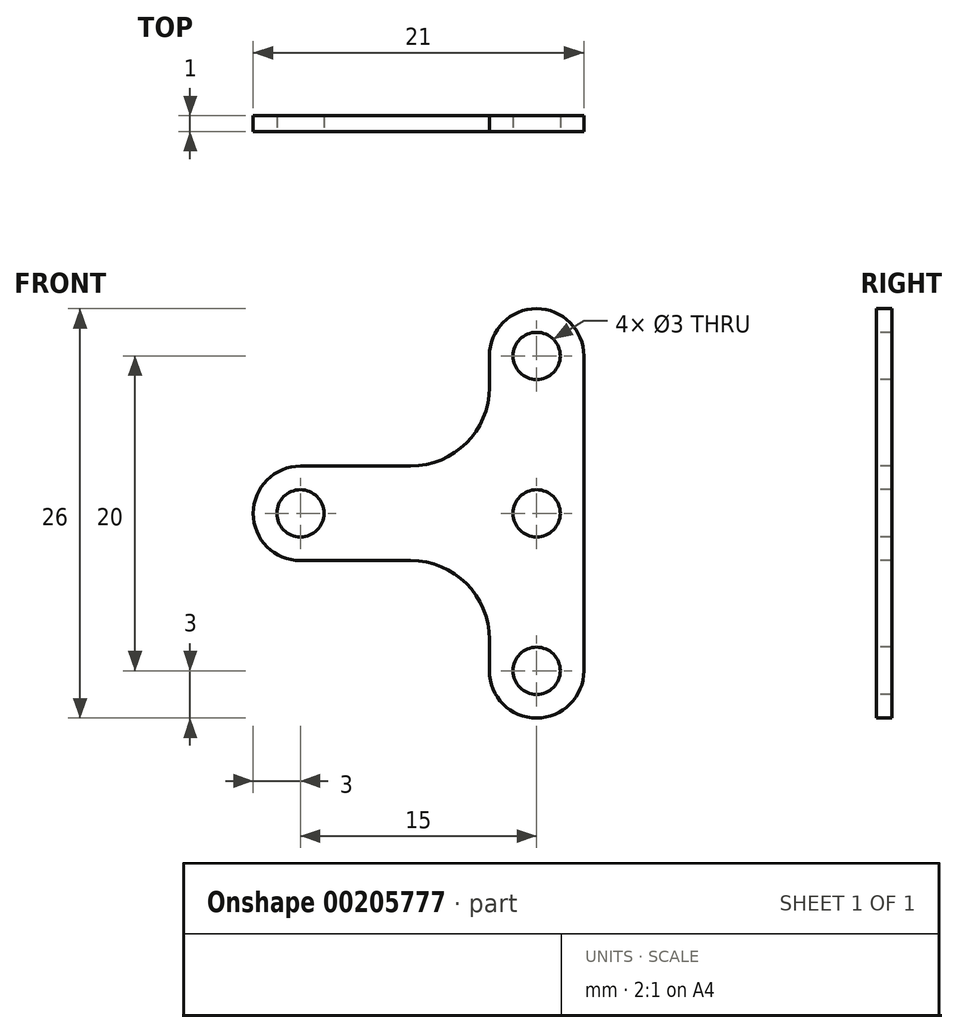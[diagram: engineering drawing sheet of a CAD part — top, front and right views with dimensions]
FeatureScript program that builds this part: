
annotation { "Feature Type Name" : "Feature", "Feature Type Description" : "" }
export const myFeature = defineFeature(function(context is Context, id is Id, definition is map)
    precondition{}
    {
        {
            var Q0;
            Q0=qCreatedBy(makeId("Front.planeOp"),FACE);
            var sketch = newSketch(context, id + "F0", { "sketchPlane" : qUnion([Q0])});
            skLineSegment(sketch, "E0", {"start": v(0, 10) * mm, "end": v(0, -10) * mm, "construction": true});
            skLineSegment(sketch, "E1", {"start": v(0, 0) * mm, "end": v(-15, 0) * mm, "construction": true});
            skCircle(sketch, "E2", {"center": v(0, 10) * mm, "radius": 1.5 * mm});
            skCircle(sketch, "E3", {"center": v(0, -10) * mm, "radius": 1.5 * mm});
            skCircle(sketch, "E4", {"center": v(-15, 0) * mm, "radius": 1.5 * mm});
            skArc(sketch, "E5.0.startCap", {"start": v(-3, 10) * mm, "mid": v(0, 13) * mm, "end": v(3, 10) * mm});
            skArc(sketch, "E5.0.endCap", {"start": v(3, -10) * mm, "mid": v(0, -13) * mm, "end": v(-3, -10) * mm});
            skLineSegment(sketch, "E5.0.left", {"start": v(3, 10) * mm, "end": v(3, -10) * mm});
            skLineSegment(sketch, "E5.0.right", {"start": v(-3, 10) * mm, "end": v(-3, 8) * mm});
            skArc(sketch, "E6.0.endCap", {"start": v(-15, -3) * mm, "mid": v(-18, 0) * mm, "end": v(-15, 3) * mm});
            skLineSegment(sketch, "E6.0.left", {"start": v(-8, -3) * mm, "end": v(-15, -3) * mm});
            skLineSegment(sketch, "E6.0.right", {"start": v(-8, 3) * mm, "end": v(-15, 3) * mm});
            skLineSegment(sketch, "E7.trimOffspring", {"start": v(-3, -8) * mm, "end": v(-3, -10) * mm});
            skPoint(sketch, "E8.visualSharp", {"position": v(-3, 3) * mm});
            skArc(sketch, "E8.filletArc", {"start": v(-8, 3) * mm, "mid": v(-4.46, 4.46) * mm, "end": v(-3, 8) * mm});
            skPoint(sketch, "E9.visualSharp", {"position": v(-3, -3) * mm});
            skArc(sketch, "E9.filletArc", {"start": v(-3, -8) * mm, "mid": v(-4.46, -4.46) * mm, "end": v(-8, -3) * mm});
            skCircle(sketch, "E10", {"center": v(0, 0) * mm, "radius": 1.5 * mm});
            skSolve(sketch);
        }
        {
            var Q0;
            Q0 = qSketchRegion(id + "F0", true);
            extrude(context, id + "F1", {"entities" : qUnion([Q0]), "oppositeDirection" : true, "depth" : 1 * mm});
        }
    });
